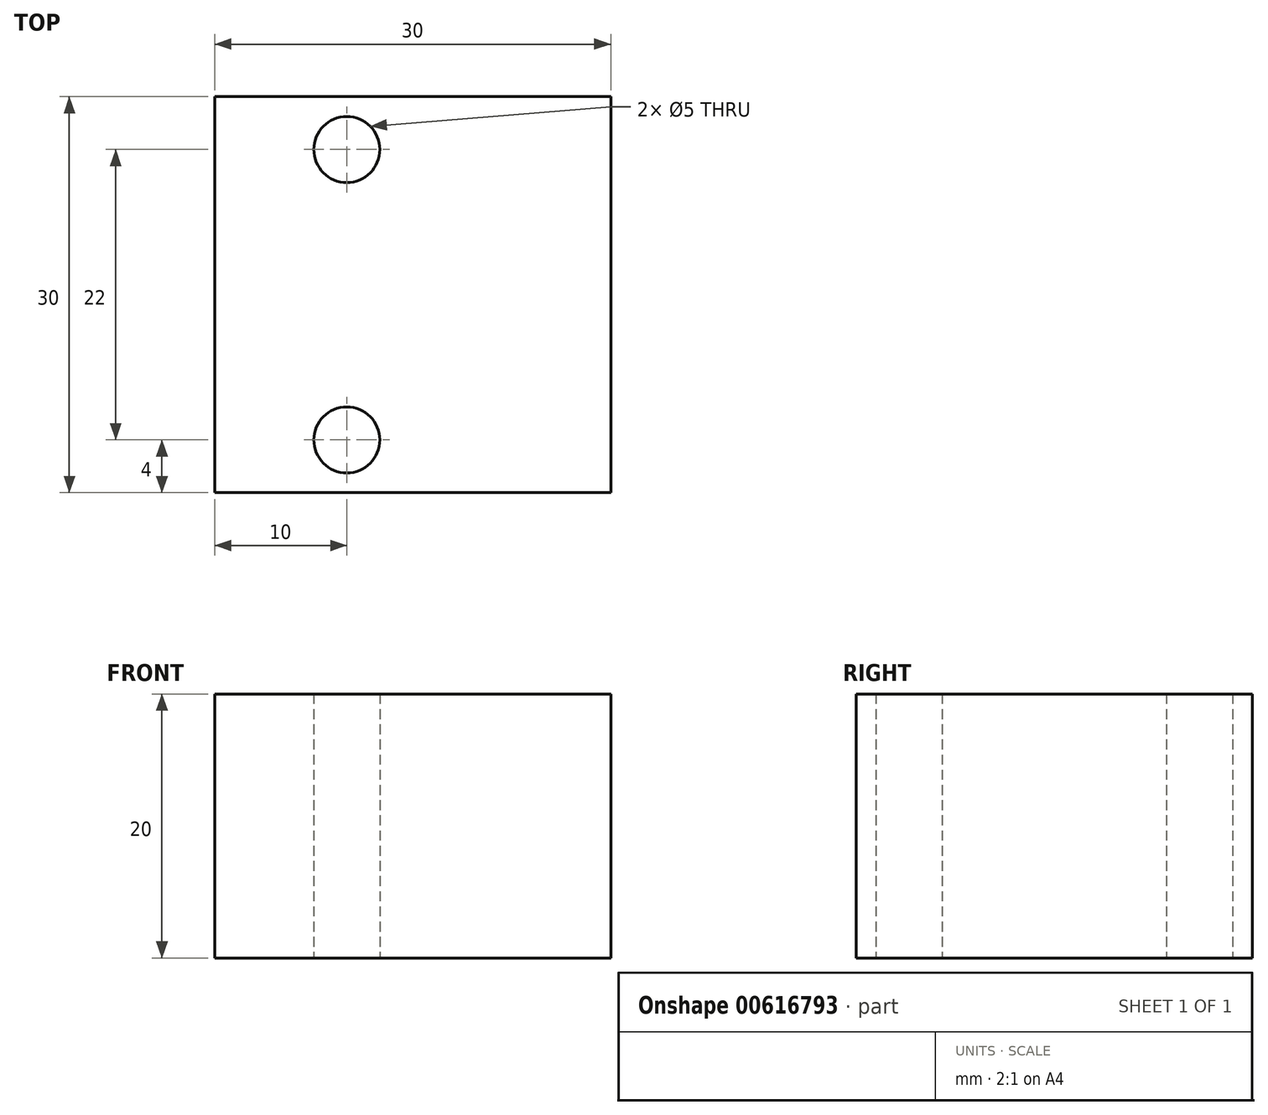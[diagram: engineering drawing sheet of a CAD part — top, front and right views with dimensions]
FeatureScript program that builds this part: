
annotation { "Feature Type Name" : "Feature", "Feature Type Description" : "" }
export const myFeature = defineFeature(function(context is Context, id is Id, definition is map)
    precondition{}
    {
        {
            var Q0;
            Q0=qCreatedBy(makeId("Top.planeOp"),FACE);
            var sketch = newSketch(context, id + "F0", { "sketchPlane" : qUnion([Q0])});
            skLineSegment(sketch, "E0.bottom", {"start": v(0, 0) * mm, "end": v(30, 0) * mm});
            skLineSegment(sketch, "E0.top", {"start": v(0, -30) * mm, "end": v(30, -30) * mm});
            skLineSegment(sketch, "E0.left", {"start": v(0, 0) * mm, "end": v(0, -30) * mm});
            skLineSegment(sketch, "E0.right", {"start": v(30, 0) * mm, "end": v(30, -30) * mm});
            skLineSegment(sketch, "E1", {"start": v(0, -15) * mm, "end": v(30, -15) * mm, "construction": true});
            skCircle(sketch, "E2", {"center": v(10, -4) * mm, "radius": 2.5 * mm});
            skCircle(sketch, "E3", {"center": v(10, -26) * mm, "radius": 2.5 * mm});
            skSolve(sketch);
        }
        {
            var Q0;
            Q0 = qSketchRegion(id + "F0", true);
            var Q1;
            Q1 = qConstructionFilter(qBodyType(qCreatedBy(id + "F0" ,EDGE), BodyType.WIRE), ConstructionObject.NO);
            extrude(context, id + "F1", {"entities" : qUnion([Q0]), "surfaceEntities" : qUnion([Q1]), "depth" : 20 * mm, "offsetDistance" : 25 * mm});
        }
    });
